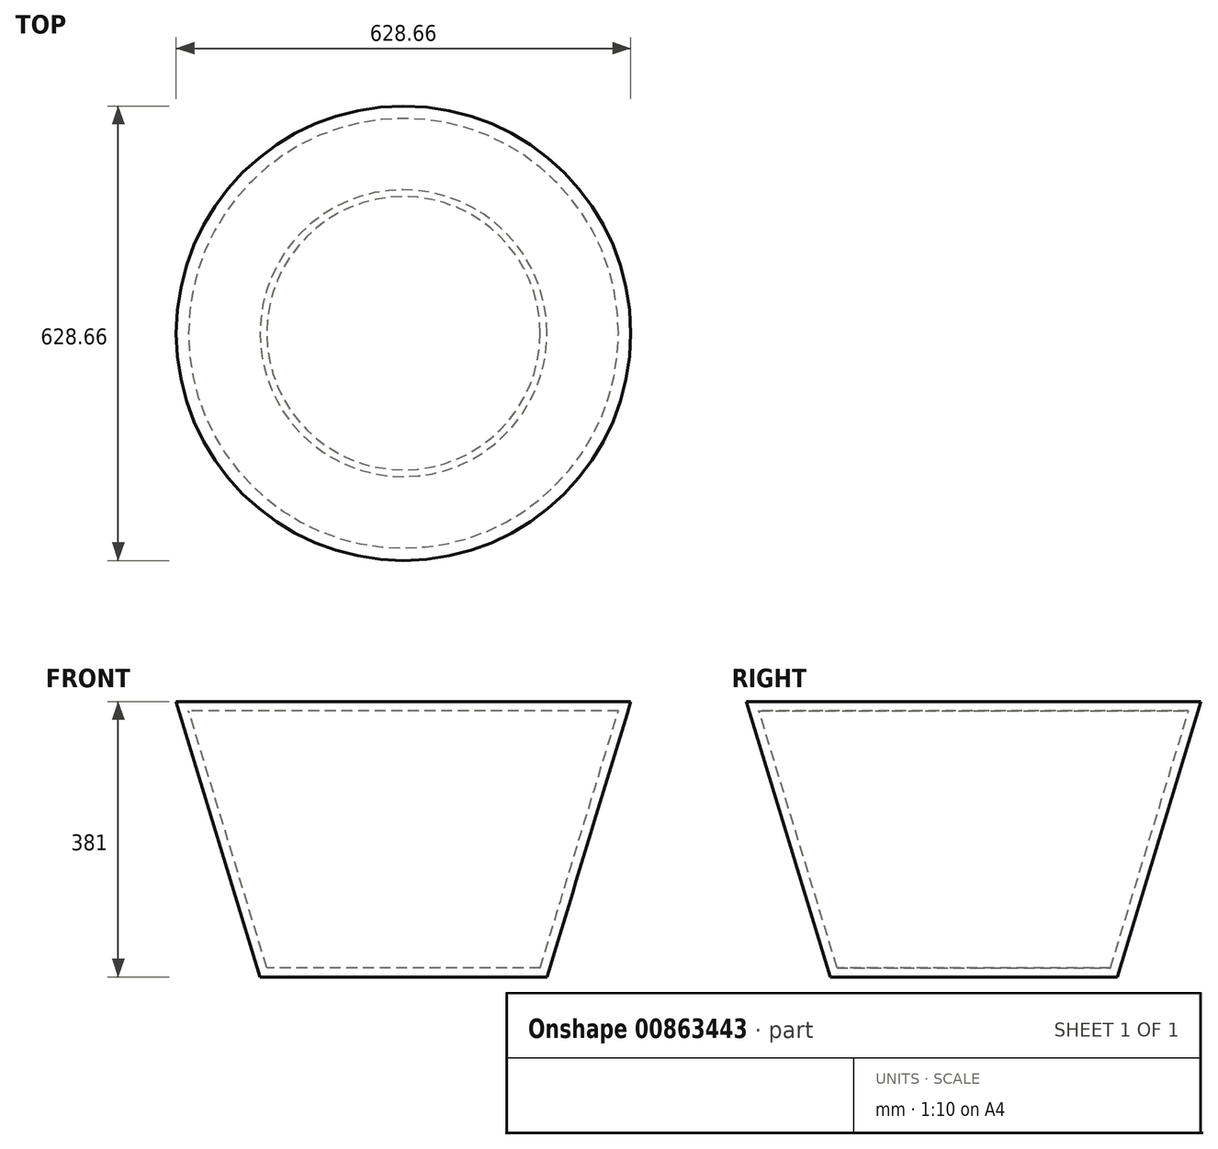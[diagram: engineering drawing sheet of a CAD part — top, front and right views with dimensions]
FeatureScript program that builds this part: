
annotation { "Feature Type Name" : "Feature", "Feature Type Description" : "" }
export const myFeature = defineFeature(function(context is Context, id is Id, definition is map)
    precondition{}
    {
        {
            var Q0;
            Q0=qCreatedBy(makeId("Top.planeOp"),FACE);
            var sketch = newSketch(context, id + "F0", { "sketchPlane" : qUnion([Q0])});
            skCircle(sketch, "E0", {"center": v(0, 0) * mm, "radius": 198.44 * mm});
            skSolve(sketch);
        }
        {
            var Q0;
            Q0=makeQuery(id+"F0.imprint","IMPRINT",FACE,{"disambiguationData":[TD([[makeQuery(id+"F0.imprint","IMPRINT",EDGE,{"derivedFrom":sQuery(id+"F0.wireOp",EDGE,"E0")}),1.0]])]});
            cPlane(context, id + "F1", {"entities" : qUnion([Q0]), "cplaneType" : CPlaneType.OFFSET, "offset" : 381 * mm, "width" : 152.4 * mm, "height" : 152.4 * mm});
        }
        {
            var Q0;
            Q0=qCreatedBy(id+"F1.planeOp",FACE);
            var sketch = newSketch(context, id + "F2", { "sketchPlane" : qUnion([Q0])});
            skCircle(sketch, "E1", {"center": v(0, 0) * mm, "radius": 314.32 * mm});
            skSolve(sketch);
        }
        {
            var Q0;
            Q0 = qSketchRegion(id + "F0", true);
            var Q1;
            Q1 = qSketchRegion(id + "F2", true);
            loft(context, id + "F3", {"sheetProfilesArray" : [{ "sheetProfileEntities" : qUnion([Q0]) }, { "sheetProfileEntities" : qUnion([Q1]) }]});
        }
        {
            var Q0;
            Q0=makeQuery(id+"F3.opLoft","CAP_FACE",FACE,{"disambiguationData":[OSD([makeQuery(id+"F2.imprint","IMPRINT",FACE,{"disambiguationData":[TD([[makeQuery(id+"F2.imprint","IMPRINT",EDGE,{"derivedFrom":sQuery(id+"F2.wireOp",EDGE,"E1")}),1.0]])]})])],"isStart":true});
            var Q1;
            Q1=makeQuery(id+"F3.opLoft","SWEPT_BODY",BODY,{"disambiguationData":[OSD([makeQuery(id+"F0.imprint","IMPRINT",FACE,{"disambiguationData":[TD([[makeQuery(id+"F0.imprint","IMPRINT",EDGE,{"derivedFrom":sQuery(id+"F0.wireOp",EDGE,"E0")}),1.0]])]}),makeQuery(id+"F2.imprint","IMPRINT",FACE,{"disambiguationData":[TD([[makeQuery(id+"F2.imprint","IMPRINT",EDGE,{"derivedFrom":sQuery(id+"F2.wireOp",EDGE,"E1")}),1.0]])]})])]});
            shell(context, id + "F4", {"isHollow" : true, "entities" : qUnion([Q0]), "parts" : qUnion([Q1]), "thickness" : 12.7 * mm});
        }
    });
